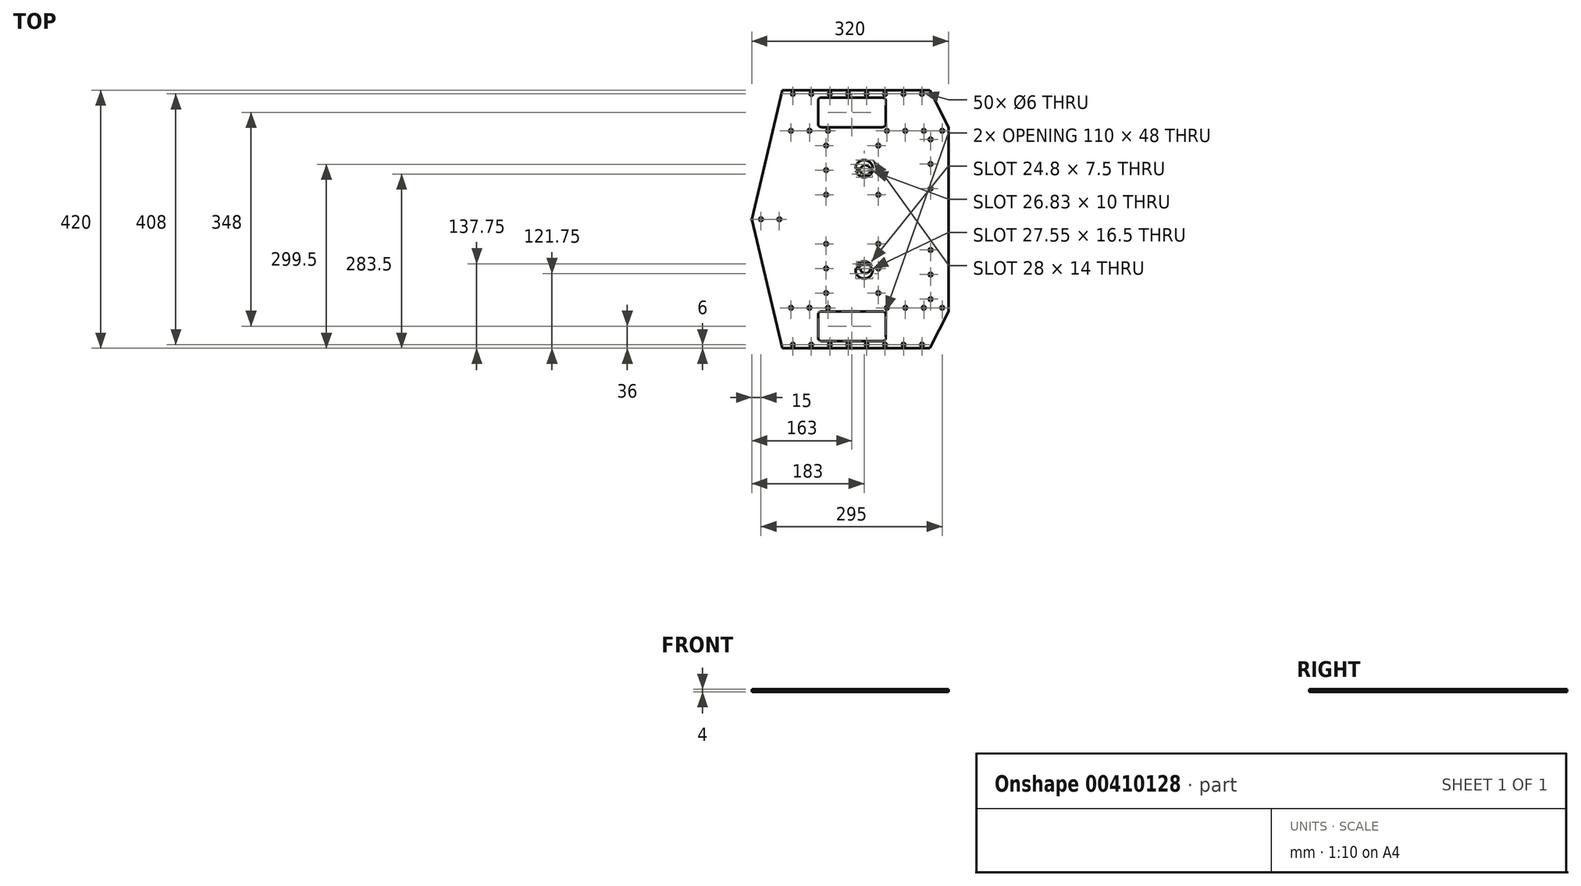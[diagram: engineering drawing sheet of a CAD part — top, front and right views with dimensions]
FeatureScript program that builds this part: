
annotation { "Feature Type Name" : "Feature", "Feature Type Description" : "" }
export const myFeature = defineFeature(function(context is Context, id is Id, definition is map)
    precondition{}
    {
        {
            var Q0;
            Q0=qCreatedBy(makeId("Top.planeOp"),FACE);
            var sketch = newSketch(context, id + "F0", { "sketchPlane" : qUnion([Q0])});
            skLineSegment(sketch, "E0.bottom", {"start": v(0, 0) * mm, "end": v(320, 0) * mm});
            skLineSegment(sketch, "E0.top", {"start": v(0, 420) * mm, "end": v(320, 420) * mm});
            skLineSegment(sketch, "E0.left", {"start": v(0, 0) * mm, "end": v(0, 420) * mm});
            skLineSegment(sketch, "E0.right", {"start": v(320, 0) * mm, "end": v(320, 420) * mm});
            skSolve(sketch);
        }
        {
            var Q0;
            Q0=qSketchRegion(id+"F0",true);
            extrude(context, id + "F1", {"entities" : qUnion([Q0]), "depth" : 4 * mm});
        }
        {
            var Q0;
            Q0=makeQuery(id+"F1.opExtrude","CAP_FACE",FACE,{"disambiguationData":[OSD([sQuery(id+"F0.wireOp",EDGE,"E0.bottom"),sQuery(id+"F0.wireOp",EDGE,"E0.top"),sQuery(id+"F0.wireOp",EDGE,"E0.left"),sQuery(id+"F0.wireOp",EDGE,"E0.right")])],"isStart":false});
            var sketch = newSketch(context, id + "F2", { "sketchPlane" : qUnion([Q0])});
            skLineSegment(sketch, "E1", {"start": v(290, 420) * mm, "end": v(320, 360) * mm});
            skLineSegment(sketch, "E2", {"start": v(290, 420) * mm, "end": v(320, 420) * mm});
            skLineSegment(sketch, "E3", {"start": v(320, 420) * mm, "end": v(320, 360) * mm});
            skLineSegment(sketch, "E4", {"start": v(290, 0) * mm, "end": v(320, 60) * mm});
            skLineSegment(sketch, "E5", {"start": v(290, 0) * mm, "end": v(320, 0) * mm});
            skLineSegment(sketch, "E6", {"start": v(320, 0) * mm, "end": v(320, 60) * mm});
            skLineSegment(sketch, "E7", {"start": v(0, 210) * mm, "end": v(320, 210) * mm, "construction": true});
            skLineSegment(sketch, "E8", {"start": v(163, 384) * mm, "end": v(163, 36) * mm, "construction": true});
            skPoint(sketch, "E9", {"position": v(163, 210) * mm});
            skLineSegment(sketch, "E10.bottom", {"start": v(213, 360) * mm, "end": v(113, 360) * mm});
            skLineSegment(sketch, "E10.top", {"start": v(213, 408) * mm, "end": v(113, 408) * mm});
            skLineSegment(sketch, "E10.left", {"start": v(218, 365) * mm, "end": v(218, 403) * mm});
            skLineSegment(sketch, "E10.right", {"start": v(108, 365) * mm, "end": v(108, 403) * mm});
            skPoint(sketch, "E10.middle", {"position": v(163, 384) * mm});
            skLineSegment(sketch, "E11.bottom", {"start": v(213, 12) * mm, "end": v(113, 12) * mm});
            skLineSegment(sketch, "E11.top", {"start": v(213, 60) * mm, "end": v(113, 60) * mm});
            skLineSegment(sketch, "E11.left", {"start": v(218, 17) * mm, "end": v(218, 55) * mm});
            skLineSegment(sketch, "E11.right", {"start": v(108, 17) * mm, "end": v(108, 55) * mm});
            skPoint(sketch, "E11.middle", {"position": v(163, 36) * mm});
            skPoint(sketch, "E12.visualSharp", {"position": v(108, 408) * mm});
            skArc(sketch, "E12.filletArc", {"start": v(113, 408) * mm, "mid": v(109.46, 406.54) * mm, "end": v(108, 403) * mm});
            skPoint(sketch, "E13.visualSharp", {"position": v(218, 408) * mm});
            skArc(sketch, "E13.filletArc", {"start": v(218, 403) * mm, "mid": v(216.54, 406.54) * mm, "end": v(213, 408) * mm});
            skPoint(sketch, "E14.visualSharp", {"position": v(108, 360) * mm});
            skArc(sketch, "E14.filletArc", {"start": v(108, 365) * mm, "mid": v(109.46, 361.46) * mm, "end": v(113, 360) * mm});
            skPoint(sketch, "E15.visualSharp", {"position": v(218, 360) * mm});
            skArc(sketch, "E15.filletArc", {"start": v(213, 360) * mm, "mid": v(216.54, 361.46) * mm, "end": v(218, 365) * mm});
            skPoint(sketch, "E16.visualSharp", {"position": v(218, 60) * mm});
            skArc(sketch, "E16.filletArc", {"start": v(218, 55) * mm, "mid": v(216.54, 58.54) * mm, "end": v(213, 60) * mm});
            skPoint(sketch, "E17.visualSharp", {"position": v(218, 12) * mm});
            skArc(sketch, "E17.filletArc", {"start": v(213, 12) * mm, "mid": v(216.54, 13.46) * mm, "end": v(218, 17) * mm});
            skPoint(sketch, "E18.visualSharp", {"position": v(108, 12) * mm});
            skArc(sketch, "E18.filletArc", {"start": v(108, 17) * mm, "mid": v(109.46, 13.46) * mm, "end": v(113, 12) * mm});
            skPoint(sketch, "E19.visualSharp", {"position": v(108, 60) * mm});
            skArc(sketch, "E19.filletArc", {"start": v(113, 60) * mm, "mid": v(109.46, 58.54) * mm, "end": v(108, 55) * mm});
            skLineSegment(sketch, "E20", {"start": v(0, 210) * mm, "end": v(50, 420) * mm});
            skLineSegment(sketch, "E21", {"start": v(0, 210) * mm, "end": v(50, 0) * mm});
            skLineSegment(sketch, "E22", {"start": v(50, 420) * mm, "end": v(0, 420) * mm});
            skLineSegment(sketch, "E23", {"start": v(0, 420) * mm, "end": v(0, 0) * mm});
            skLineSegment(sketch, "E24", {"start": v(0, 0) * mm, "end": v(50, 0) * mm});
            skSolve(sketch);
        }
        {
            var Q0;
            Q0=qSketchRegion(id+"F2",true);
            var Q1;
            Q1=makeQuery(id+"F1.opExtrude","CAP_FACE",FACE,{"disambiguationData":[OSD([sQuery(id+"F0.wireOp",EDGE,"E0.bottom"),sQuery(id+"F0.wireOp",EDGE,"E0.top"),sQuery(id+"F0.wireOp",EDGE,"E0.left"),sQuery(id+"F0.wireOp",EDGE,"E0.right")])],"isStart":true});
            extrude(context, id + "F3", {"entities" : qUnion([Q0]), "operationType" : NewBodyOperationType.REMOVE, "endBound" : BoundingType.UP_TO_SURFACE, "oppositeDirection" : true, "endBoundEntityFace" : qUnion([Q1]), "depth" : 25 * mm});
        }
        {
            var Q0;
            Q0=makeQuery(id+"F1.opExtrude","CAP_FACE",FACE,{"disambiguationData":[OSD([sQuery(id+"F0.wireOp",EDGE,"E0.bottom"),sQuery(id+"F0.wireOp",EDGE,"E0.top"),sQuery(id+"F0.wireOp",EDGE,"E0.left"),sQuery(id+"F0.wireOp",EDGE,"E0.right")])],"isStart":false});
            var sketch = newSketch(context, id + "F4", { "sketchPlane" : qUnion([Q0])});
            skLineSegment(sketch, "E25", {"start": v(67, 6) * mm, "end": v(277, 6) * mm, "construction": true});
            skCircle(sketch, "E26", {"center": v(67, 6) * mm, "radius": 3 * mm});
            skCircle(sketch, "E27.1.0.0", {"center": v(97, 6) * mm, "radius": 3 * mm});
            skCircle(sketch, "E27.2.0.0", {"center": v(127, 6) * mm, "radius": 3 * mm});
            skCircle(sketch, "E27.3.0.0", {"center": v(157, 6) * mm, "radius": 3 * mm});
            skCircle(sketch, "E27.4.0.0", {"center": v(187, 6) * mm, "radius": 3 * mm});
            skCircle(sketch, "E27.5.0.0", {"center": v(217, 6) * mm, "radius": 3 * mm});
            skCircle(sketch, "E27.6.0.0", {"center": v(247, 6) * mm, "radius": 3 * mm});
            skCircle(sketch, "E27.7.0.0", {"center": v(277, 6) * mm, "radius": 3 * mm});
            skLineSegment(sketch, "E27.direction1", {"start": v(67, 6) * mm, "end": v(97, 6) * mm, "construction": true});
            skLineSegment(sketch, "E28", {"start": v(70, 66) * mm, "end": v(310, 66) * mm, "construction": true});
            skCircle(sketch, "E29", {"center": v(64, 66) * mm, "radius": 3 * mm});
            skCircle(sketch, "E30.1.0.0", {"center": v(94, 66) * mm, "radius": 3 * mm});
            skCircle(sketch, "E30.2.0.0", {"center": v(124, 66) * mm, "radius": 3 * mm});
            skCircle(sketch, "E30.3.0.0", {"center": v(160, 66) * mm, "radius": 3 * mm, "construction": true});
            skCircle(sketch, "E30.4.0.0", {"center": v(190, 66) * mm, "radius": 3 * mm, "construction": true});
            skCircle(sketch, "E30.5.0.0", {"center": v(220, 66) * mm, "radius": 3 * mm});
            skCircle(sketch, "E30.6.0.0", {"center": v(250, 66) * mm, "radius": 3 * mm});
            skCircle(sketch, "E30.7.0.0", {"center": v(280, 66) * mm, "radius": 3 * mm});
            skCircle(sketch, "E30.8.0.0", {"center": v(310, 66) * mm, "radius": 3 * mm});
            skLineSegment(sketch, "E30.direction1", {"start": v(64, 66) * mm, "end": v(94, 66) * mm, "construction": true});
            skLineSegment(sketch, "E31", {"start": v(0, 210) * mm, "end": v(320, 210) * mm, "construction": true});
            skCircle(sketch, "E32.MirrorC", {"center": v(67, 414) * mm, "radius": 3 * mm});
            skCircle(sketch, "E33.MirrorC", {"center": v(64, 354) * mm, "radius": 3 * mm});
            skCircle(sketch, "E34.MirrorC", {"center": v(97, 414) * mm, "radius": 3 * mm});
            skCircle(sketch, "E35.MirrorC", {"center": v(310, 354) * mm, "radius": 3 * mm});
            skCircle(sketch, "E36.MirrorC", {"center": v(277, 414) * mm, "radius": 3 * mm});
            skCircle(sketch, "E37.MirrorC", {"center": v(94, 354) * mm, "radius": 3 * mm});
            skCircle(sketch, "E38.MirrorC", {"center": v(220, 354) * mm, "radius": 3 * mm});
            skLineSegment(sketch, "E39.MirrorCS", {"start": v(64, 354) * mm, "end": v(94, 354) * mm, "construction": true});
            skCircle(sketch, "E40.MirrorC", {"center": v(280, 354) * mm, "radius": 3 * mm});
            skCircle(sketch, "E41.MirrorC", {"center": v(124, 354) * mm, "radius": 3 * mm});
            skCircle(sketch, "E42.MirrorC", {"center": v(160, 354) * mm, "radius": 3 * mm, "construction": true});
            skCircle(sketch, "E43.MirrorC", {"center": v(190, 354) * mm, "radius": 3 * mm, "construction": true});
            skCircle(sketch, "E44.MirrorC", {"center": v(127, 414) * mm, "radius": 3 * mm});
            skCircle(sketch, "E45.MirrorC", {"center": v(250, 354) * mm, "radius": 3 * mm});
            skCircle(sketch, "E46.MirrorC", {"center": v(157, 414) * mm, "radius": 3 * mm});
            skCircle(sketch, "E47.MirrorC", {"center": v(187, 414) * mm, "radius": 3 * mm});
            skCircle(sketch, "E48.MirrorC", {"center": v(217, 414) * mm, "radius": 3 * mm});
            skCircle(sketch, "E49.MirrorC", {"center": v(247, 414) * mm, "radius": 3 * mm});
            skLineSegment(sketch, "E50.MirrorCS", {"start": v(67, 414) * mm, "end": v(277, 414) * mm, "construction": true});
            skLineSegment(sketch, "E51.MirrorCS", {"start": v(67, 414) * mm, "end": v(97, 414) * mm, "construction": true});
            skLineSegment(sketch, "E52.MirrorCS", {"start": v(70, 354) * mm, "end": v(310, 354) * mm, "construction": true});
            skSolve(sketch);
        }
        {
            var Q0;
            Q0 = qSketchRegion(id + "F4", true);
            extrude(context, id + "F5", {"entities" : qUnion([Q0]), "operationType" : NewBodyOperationType.REMOVE, "oppositeDirection" : true, "depth" : 25 * mm});
        }
        {
            var Q0;
            Q0=makeQuery(id+"F1.opExtrude","CAP_FACE",FACE,{"disambiguationData":[OSD([sQuery(id+"F0.wireOp",EDGE,"E0.bottom"),sQuery(id+"F0.wireOp",EDGE,"E0.top"),sQuery(id+"F0.wireOp",EDGE,"E0.left"),sQuery(id+"F0.wireOp",EDGE,"E0.right")])],"isStart":false});
            var sketch = newSketch(context, id + "F6", { "sketchPlane" : qUnion([Q0])});
            skLineSegment(sketch, "E53", {"start": v(0, 210) * mm, "end": v(320, 210) * mm, "construction": true});
            skLineSegment(sketch, "E54", {"start": v(108, 365) * mm, "end": v(108, 55) * mm, "construction": true});
            skLineSegment(sketch, "E55", {"start": v(121, 90) * mm, "end": v(121, 330.2) * mm, "construction": true});
            skCircle(sketch, "E56", {"center": v(121, 90) * mm, "radius": 3 * mm});
            skCircle(sketch, "E57.0.1.0", {"center": v(121, 130) * mm, "radius": 3 * mm});
            skCircle(sketch, "E57.0.2.0", {"center": v(121, 170) * mm, "radius": 3 * mm});
            skCircle(sketch, "E57.1.0.0", {"center": v(206, 90) * mm, "radius": 3 * mm});
            skCircle(sketch, "E57.1.1.0", {"center": v(206, 130) * mm, "radius": 3 * mm});
            skCircle(sketch, "E57.1.2.0", {"center": v(206, 170) * mm, "radius": 3 * mm});
            skCircle(sketch, "E57.2.0.0", {"center": v(291, 80) * mm, "radius": 3 * mm});
            skCircle(sketch, "E57.2.1.0", {"center": v(291, 120) * mm, "radius": 3 * mm});
            skCircle(sketch, "E57.2.2.0", {"center": v(291, 160) * mm, "radius": 3 * mm});
            skLineSegment(sketch, "E57.direction1", {"start": v(121, 90) * mm, "end": v(206, 90) * mm, "construction": true});
            skLineSegment(sketch, "E57.direction2", {"start": v(121, 90) * mm, "end": v(121, 130) * mm, "construction": true});
            skCircle(sketch, "E58.MirrorC", {"center": v(121, 330) * mm, "radius": 3 * mm});
            skCircle(sketch, "E59.MirrorC", {"center": v(121, 290) * mm, "radius": 3 * mm});
            skCircle(sketch, "E60.MirrorC", {"center": v(206, 330) * mm, "radius": 3 * mm});
            skCircle(sketch, "E61.MirrorC", {"center": v(206, 250) * mm, "radius": 3 * mm});
            skCircle(sketch, "E62.MirrorC", {"center": v(291, 340) * mm, "radius": 3 * mm});
            skCircle(sketch, "E63.MirrorC", {"center": v(121, 250) * mm, "radius": 3 * mm});
            skCircle(sketch, "E64.MirrorC", {"center": v(206, 290) * mm, "radius": 3 * mm});
            skCircle(sketch, "E65.MirrorC", {"center": v(291, 300) * mm, "radius": 3 * mm});
            skCircle(sketch, "E66.MirrorC", {"center": v(291, 260) * mm, "radius": 3 * mm});
            skLineSegment(sketch, "E67.MirrorCS", {"start": v(121, 330) * mm, "end": v(121, 290) * mm, "construction": true});
            skLineSegment(sketch, "E68.MirrorCS", {"start": v(121, 330) * mm, "end": v(206, 330) * mm, "construction": true});
            skSolve(sketch);
        }
        {
            var Q0;
            Q0 = qSketchRegion(id + "F6", true);
            extrude(context, id + "F7", {"entities" : qUnion([Q0]), "operationType" : NewBodyOperationType.REMOVE, "oppositeDirection" : true, "depth" : 25 * mm});
        }
        {
            var Q0;
            Q0=makeQuery(id+"F1.opExtrude","CAP_FACE",FACE,{"disambiguationData":[OSD([sQuery(id+"F0.wireOp",EDGE,"E0.bottom"),sQuery(id+"F0.wireOp",EDGE,"E0.top"),sQuery(id+"F0.wireOp",EDGE,"E0.left"),sQuery(id+"F0.wireOp",EDGE,"E0.right")])],"isStart":false});
            var sketch = newSketch(context, id + "F8", { "sketchPlane" : qUnion([Q0])});
            skLineSegment(sketch, "E69", {"start": v(0, 210) * mm, "end": v(320, 210) * mm, "construction": true});
            skCircle(sketch, "E70", {"center": v(15, 210) * mm, "radius": 3 * mm});
            skCircle(sketch, "E71.1.0.0", {"center": v(45, 210) * mm, "radius": 3 * mm});
            skLineSegment(sketch, "E71.direction1", {"start": v(15, 210) * mm, "end": v(45, 210) * mm, "construction": true});
            skSolve(sketch);
        }
        {
            var Q0;
            Q0 = qSketchRegion(id + "F8", true);
            extrude(context, id + "F9", {"entities" : qUnion([Q0]), "operationType" : NewBodyOperationType.REMOVE, "oppositeDirection" : true, "depth" : 25 * mm});
        }
        {
            var Q0;
            Q0=makeQuery(id+"F1.opExtrude","CAP_FACE",FACE,{"disambiguationData":[OSD([sQuery(id+"F0.wireOp",EDGE,"E0.bottom"),sQuery(id+"F0.wireOp",EDGE,"E0.top"),sQuery(id+"F0.wireOp",EDGE,"E0.left"),sQuery(id+"F0.wireOp",EDGE,"E0.right")])],"isStart":false});
            var sketch = newSketch(context, id + "F10", { "sketchPlane" : qUnion([Q0])});
            skLineSegment(sketch, "E72", {"start": v(320, 210) * mm, "end": v(0, 210) * mm, "construction": true});
            skLineSegment(sketch, "E73", {"start": v(185, 130) * mm, "end": v(185, 290) * mm, "construction": true});
            skPoint(sketch, "E74", {"position": v(185, 210) * mm});
            skArc(sketch, "E75", {"start": v(177.14, 288.5) * mm, "mid": v(185, 282) * mm, "end": v(192.86, 288.5) * mm});
            skArc(sketch, "E76", {"start": v(177, 130) * mm, "mid": v(185, 122) * mm, "end": v(193, 130) * mm});
            skLineSegment(sketch, "E77", {"start": v(183, 127.5) * mm, "end": v(183, 292.5) * mm, "construction": true});
            skArc(sketch, "E78", {"start": v(169.58, 288.5) * mm, "mid": v(183, 278.5) * mm, "end": v(196.42, 288.5) * mm});
            skArc(sketch, "E79", {"start": v(169.23, 130) * mm, "mid": v(183, 113.5) * mm, "end": v(196.77, 130) * mm});
            skPoint(sketch, "E80", {"position": v(183, 210) * mm});
            skLineSegment(sketch, "E81.bottom", {"start": v(169.23, 130) * mm, "end": v(177, 130) * mm});
            skLineSegment(sketch, "E81.top", {"start": v(170.6, 134) * mm, "end": v(178.07, 134) * mm});
            skLineSegment(sketch, "E82.bottom", {"start": v(169, 292.5) * mm, "end": v(177.4, 292.5) * mm});
            skLineSegment(sketch, "E82.top", {"start": v(169.58, 288.5) * mm, "end": v(177.14, 288.5) * mm});
            skLineSegment(sketch, "E83", {"start": v(162.95, 134) * mm, "end": v(162.95, 288.5) * mm, "construction": true});
            skLineSegment(sketch, "E84.trimOffspring", {"start": v(192.86, 288.5) * mm, "end": v(196.42, 288.5) * mm});
            skLineSegment(sketch, "E85.trimOffspring", {"start": v(192.6, 292.5) * mm, "end": v(197, 292.5) * mm});
            skArc(sketch, "E86.trimOffspring", {"start": v(192.6, 292.5) * mm, "mid": v(185, 298) * mm, "end": v(177.4, 292.5) * mm});
            skArc(sketch, "E87.trimOffspring", {"start": v(197, 292.5) * mm, "mid": v(183, 306.5) * mm, "end": v(169, 292.5) * mm});
            skArc(sketch, "E88.trimOffspring", {"start": v(191.93, 134) * mm, "mid": v(185, 138) * mm, "end": v(178.07, 134) * mm});
            skArc(sketch, "E89.trimOffspring", {"start": v(195.4, 134) * mm, "mid": v(183, 141.5) * mm, "end": v(170.6, 134) * mm});
            skLineSegment(sketch, "E90.trimOffspring", {"start": v(193, 130) * mm, "end": v(196.77, 130) * mm});
            skLineSegment(sketch, "E91.trimOffspring", {"start": v(191.93, 134) * mm, "end": v(195.4, 134) * mm});
            skPoint(sketch, "E81.left.start.orphan", {"position": v(162.95, 130) * mm});
            skPoint(sketch, "E92.orphan", {"position": v(162.95, 292.5) * mm});
            skSolve(sketch);
        }
        {
            var Q0;
            Q0 = qSketchRegion(id + "F10", true);
            extrude(context, id + "F11", {"entities" : qUnion([Q0]), "operationType" : NewBodyOperationType.REMOVE, "oppositeDirection" : true, "depth" : 25 * mm});
        }
    });
